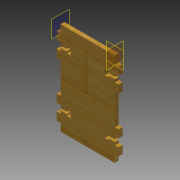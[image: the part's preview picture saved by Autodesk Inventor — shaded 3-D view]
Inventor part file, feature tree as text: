
AUTODESK INVENTOR PART (.ipt)
format: ipt  version: 2014 (Build 180170000, 170)  size: 239,616 bytes
history: native  units: mm
features: sketch x4, plane x3, extrude x3
ambient origin geometry x8: Origin, YZ Plane, XZ Plane, XY Plane, X Axis, Y Axis, Z Axis, Center Point
bodies: Body1 (feature_tree)
feature tree (10):
  sketch  "Sketch1"  dims[d46=10.0mm d47=5.0mm]
  plane  "Work Plane2"
  sketch  "Sketch2"  dims[d48=10.0mm d49=10.0mm]
  plane  "Work Plane3"
  sketch  "Sketch3"  dims[d50=10.0mm d58=10.0mm]
  plane  "Work Plane1"
  sketch  "Sketch4"  dims[d59=5.0mm d60=10.0mm d61=10.0mm d62=10.0mm d70=120.0mm d72=5.0mm d73=0.0mm d75=5.0mm d76=10.0mm d77=10.0mm d78=5.0mm d79=10.0mm d80=40.0mm d81=10.0mm d82=10.0mm d83=10.0mm d84=5.0mm d85=0.0mm d86=5.0mm d87=0.0mm d115=5.0mm d116=7.0mm d117=5.0mm d119=8.0mm d120=2.0mm d121=5.0mm d123=25.0mm d124=1.5mm d125=1.5mm d126=1.5mm d127=1.5mm d128=35.0mm d129=40.0mm d130=70.0mm d131=8.0mm d132=2.0mm]
  extrude  "Extrusion12"  Depth=5.0mm
  extrude  "Extrusion13"  Depth=10.0mm
  extrude  "Extrusion14"  Depth=10.0mm
